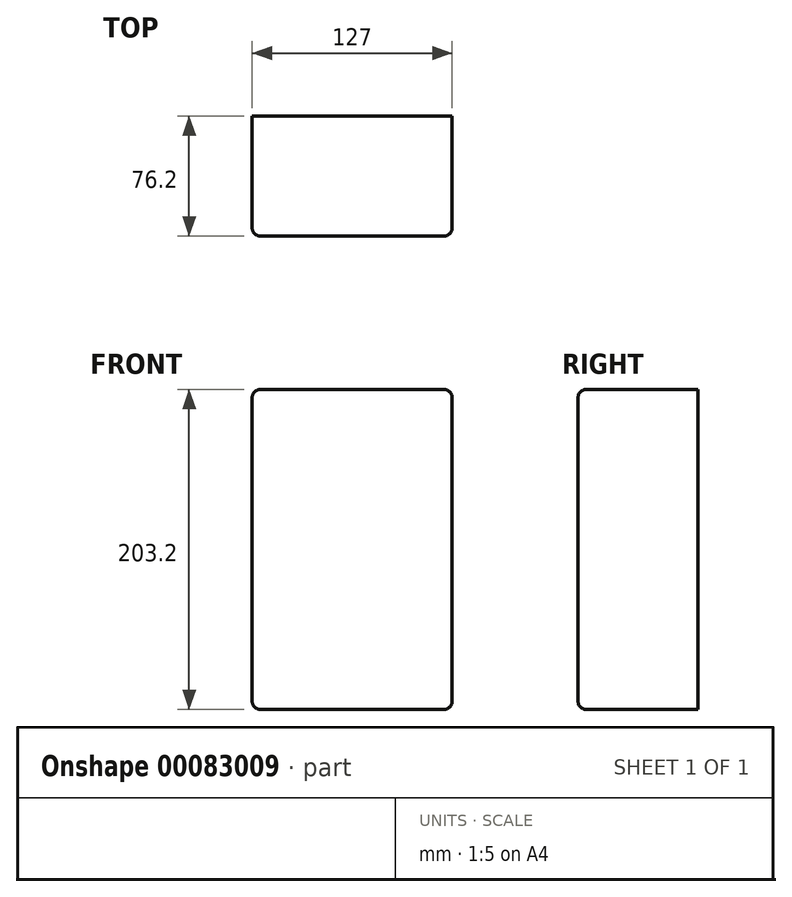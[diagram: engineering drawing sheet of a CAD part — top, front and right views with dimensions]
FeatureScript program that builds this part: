
annotation { "Feature Type Name" : "Feature", "Feature Type Description" : "" }
export const myFeature = defineFeature(function(context is Context, id is Id, definition is map)
    precondition{}
    {
        {
            var Q0;
            Q0=qCreatedBy(makeId("Top.planeOp"),FACE);
            var sketch = newSketch(context, id + "F0", { "sketchPlane" : qUnion([Q0])});
            skLineSegment(sketch, "E0.bottom", {"start": v(-146.4, 106.56) * mm, "end": v(-19.4, 106.56) * mm});
            skLineSegment(sketch, "E0.top", {"start": v(-146.4, 30.36) * mm, "end": v(-19.4, 30.36) * mm});
            skLineSegment(sketch, "E0.left", {"start": v(-146.4, 106.56) * mm, "end": v(-146.4, 30.36) * mm});
            skLineSegment(sketch, "E0.right", {"start": v(-19.4, 106.56) * mm, "end": v(-19.4, 30.36) * mm});
            skSolve(sketch);
        }
        {
            var Q0;
            Q0=makeQuery(id+"F0.imprint","IMPRINT",FACE,{"disambiguationData":[TD([[makeQuery(id+"F0.imprint","IMPRINT",EDGE,{"derivedFrom":sQuery(id+"F0.wireOp",EDGE,"E0.bottom")}),-1.0]])]});
            extrude(context, id + "F1", {"entities" : qUnion([Q0]), "depth" : 203.2 * mm});
        }
        {
            var Q0;
            Q0=makeQuery(id+"F1.opExtrude","SWEPT_EDGE",EDGE,{"disambiguationData":[OSD([sQuery(id+"F0.wireOp",EDGE,"E0.top"),sQuery(id+"F0.wireOp",EDGE,"E0.right")])]});
            var Q1;
            Q1=makeQuery(id+"F1.opExtrude","CAP_EDGE",EDGE,{"disambiguationData":[OSD([sQuery(id+"F0.wireOp",EDGE,"E0.right")])],"isStart":false});
            var Q2;
            Q2=makeQuery(id+"F1.opExtrude","CAP_EDGE",EDGE,{"disambiguationData":[OSD([sQuery(id+"F0.wireOp",EDGE,"E0.top")])],"isStart":false});
            var Q3;
            Q3=makeQuery(id+"F1.opExtrude","SWEPT_EDGE",EDGE,{"disambiguationData":[OSD([sQuery(id+"F0.wireOp",EDGE,"E0.top"),sQuery(id+"F0.wireOp",EDGE,"E0.left")])]});
            var Q4;
            Q4=makeQuery(id+"F1.opExtrude","CAP_EDGE",EDGE,{"disambiguationData":[OSD([sQuery(id+"F0.wireOp",EDGE,"E0.left")])],"isStart":false});
            var Q5;
            Q5=makeQuery(id+"F1.opExtrude","CAP_EDGE",EDGE,{"disambiguationData":[OSD([sQuery(id+"F0.wireOp",EDGE,"E0.top")])],"isStart":true});
            var Q6;
            Q6=makeQuery(id+"F1.opExtrude","CAP_EDGE",EDGE,{"disambiguationData":[OSD([sQuery(id+"F0.wireOp",EDGE,"E0.right")])],"isStart":true});
            var Q7;
            Q7=makeQuery(id+"F1.opExtrude","CAP_EDGE",EDGE,{"disambiguationData":[OSD([sQuery(id+"F0.wireOp",EDGE,"E0.left")])],"isStart":true});
            fillet(context, id + "F2", {"entities" : qUnion([Q0, Q1, Q2, Q3, Q4, Q5, Q6, Q7]), "radius" : 5.08 * mm, "tangentPropagation" : true, "allowEdgeOverflow" : false});
        }
    });
